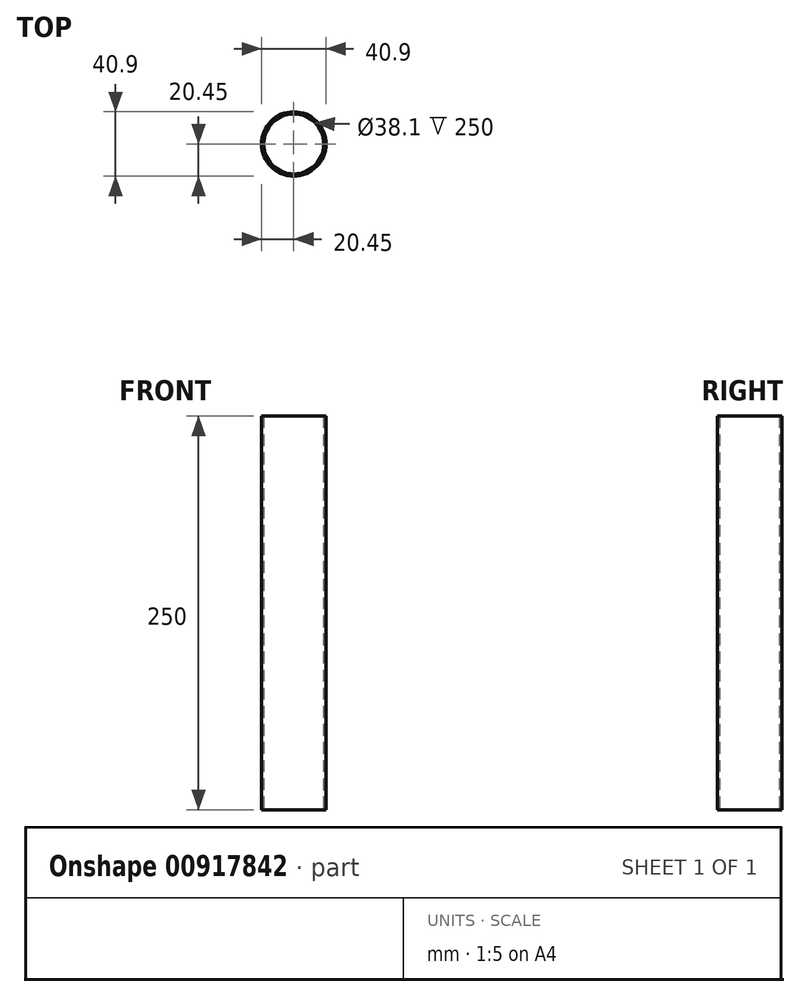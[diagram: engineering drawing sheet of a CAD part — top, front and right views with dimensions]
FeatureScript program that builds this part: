
annotation { "Feature Type Name" : "Feature", "Feature Type Description" : "" }
export const myFeature = defineFeature(function(context is Context, id is Id, definition is map)
    precondition{}
    {
        {
            var Q0;
            Q0=qCreatedBy(makeId("Top.planeOp"),FACE);
            var sketch = newSketch(context, id + "F0", { "sketchPlane" : qUnion([Q0])});
            skCircle(sketch, "E0", {"center": v(0, 0) * mm, "radius": 20.45 * mm});
            skCircle(sketch, "E1", {"center": v(0, 0) * mm, "radius": 19.05 * mm});
            skSolve(sketch);
        }
        {
            var Q0;
            Q0=makeQuery(id+"F0.imprint","IMPRINT",FACE,{"disambiguationData":[TD([[makeQuery(id+"F0.imprint","IMPRINT",EDGE,{"derivedFrom":sQuery(id+"F0.wireOp",EDGE,"E0")}),1.0]])]});
            extrude(context, id + "F1", {"entities" : qUnion([Q0]), "depth" : 250 * mm, "offsetDistance" : 25 * mm});
        }
    });
